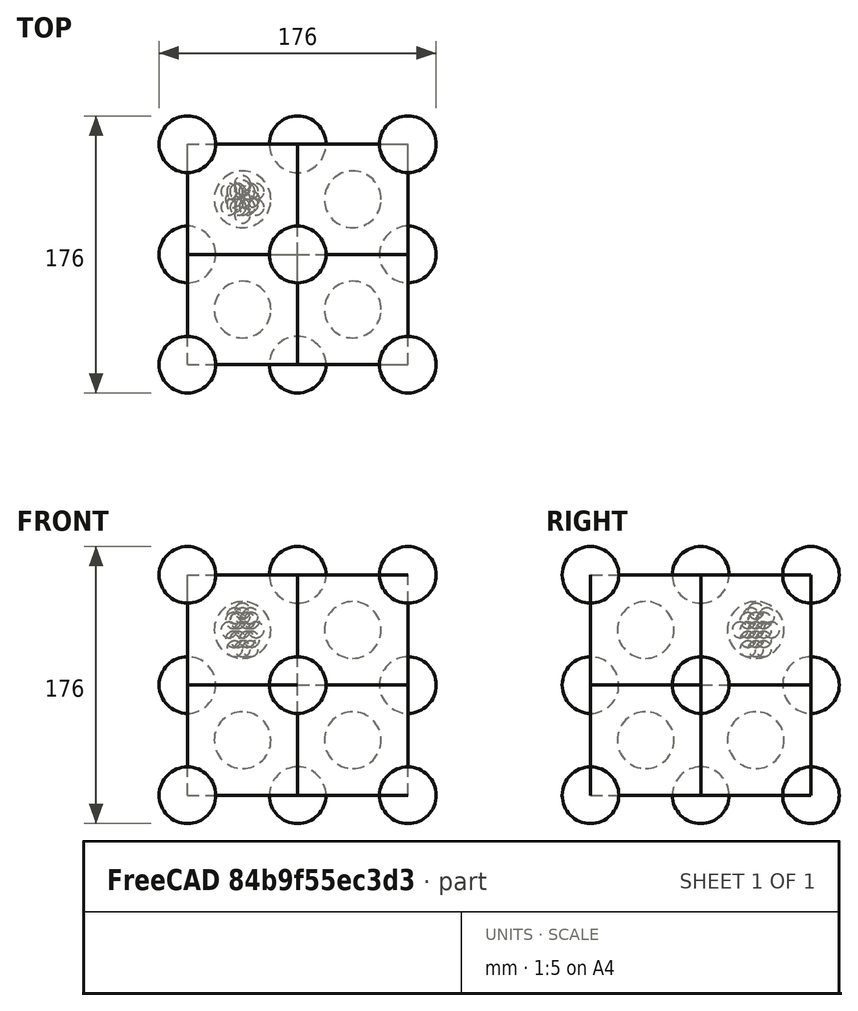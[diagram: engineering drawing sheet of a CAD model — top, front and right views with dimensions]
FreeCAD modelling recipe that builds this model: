
FCSTD DOCUMENT  (FreeCAD 0.16R6707 (Git))
Label: si-cristal
License: All rights reserved
LicenseURL: http://en.wikipedia.org/wiki/All_rights_reserved
objects: Part::Feature×45, Part::Sphere×10, Part::Part2DObjectPython×4, App::DocumentObjectGroup×2, Part::Box×1, Part::FeaturePython×1
note: 61 computed .brp shape members not serialized (recipe doc carries the construction recipe); baked Part::Feature solids carry a one-line shape summary decoded from their .brp

FEATURE [Part::Feature] Sphere001
  Placement = pos=(0,-10,0) rot=(0,0,1;0rad)
  shape: bbox 10 x 10 x 10 mm, 1 faces (baked)
FEATURE [Part::Feature] Sphere002
  Placement = pos=(-8.66025,-5,0) rot=(0,0,1;0rad)
  shape: bbox 10 x 10 x 10 mm, 1 faces (baked)
FEATURE [Part::Feature] Sphere003
  Placement = pos=(-8.66025,5,0) rot=(0,0,1;0rad)
  shape: bbox 10 x 10 x 10 mm, 1 faces (baked)
FEATURE [Part::Feature] Sphere004
  Placement = pos=(8.66025,-5,0) rot=(0,0,1;0rad)
  shape: bbox 10 x 10 x 10 mm, 1 faces (baked)
FEATURE [Part::Feature] Sphere005
  Placement = pos=(8.66025,5,0) rot=(0,0,1;0rad)
  shape: bbox 10 x 10 x 10 mm, 1 faces (baked)
FEATURE [Part::Feature] Sphere006
  Placement = pos=(4e-12,10,0) rot=(0,0,1;0rad)
  shape: bbox 10 x 10 x 10 mm, 1 faces (baked)
FEATURE [Part::Sphere] Sphere007  label="Center"
  Angle1 = -90
  Angle2 = 90
  Angle3 = 360
  Radius = 5
FEATURE [Part::Feature] Sphere  label="Sphere030"
  Placement = pos=(-3,5,6) rot=(0,0,1;0rad)
  shape: bbox 10 x 10 x 10 mm, 1 faces (baked)
FEATURE [Part::Feature] Sphere008  label="Sphere031"
  Placement = pos=(2.83013,5.09808,6) rot=(0,0,1;0rad)
  shape: bbox 10 x 10 x 10 mm, 1 faces (baked)
FEATURE [Part::Feature] Sphere009  label="Sphere032"
  Placement = pos=(5.83013,0.0980762,6) rot=(0,0,1;0rad)
  shape: bbox 10 x 10 x 10 mm, 1 faces (baked)
FEATURE [Part::Feature] Sphere010  label="Sphere033"
  Placement = pos=(3,-5,6) rot=(0,0,1;0rad)
  shape: bbox 10 x 10 x 10 mm, 1 faces (baked)
FEATURE [Part::Feature] Sphere011  label="Sphere034"
  Placement = pos=(-2.83013,-5.09808,6) rot=(0,0,1;0rad)
  shape: bbox 10 x 10 x 10 mm, 1 faces (baked)
FEATURE [Part::Feature] Sphere012  label="Sphere035"
  Placement = pos=(-5.83013,-0.0980762,6) rot=(0,0,1;0rad)
  shape: bbox 10 x 10 x 10 mm, 1 faces (baked)
FEATURE [Part::Feature] Sphere013  label="Sphere036"
  Placement = pos=(-3,5,-6) rot=(0,0,1;0rad)
  shape: bbox 10 x 10 x 10 mm, 1 faces (baked)
FEATURE [Part::Feature] Sphere014  label="Sphere037"
  Placement = pos=(2.83013,5.09808,-6) rot=(0,0,1;0rad)
  shape: bbox 10 x 10 x 10 mm, 1 faces (baked)
FEATURE [Part::Feature] Sphere015  label="Sphere038"
  Placement = pos=(-2.83013,-5.09808,-6) rot=(0,0,1;0rad)
  shape: bbox 10 x 10 x 10 mm, 1 faces (baked)
FEATURE [Part::Feature] Sphere016  label="Sphere039"
  Placement = pos=(5.83013,0.0980762,-6) rot=(0,0,1;0rad)
  shape: bbox 10 x 10 x 10 mm, 1 faces (baked)
FEATURE [Part::Feature] Sphere017  label="Sphere015"
  Placement = pos=(3,-5,-6) rot=(0,0,1;0rad)
  shape: bbox 10 x 10 x 10 mm, 1 faces (baked)
FEATURE [Part::Feature] Sphere018  label="Sphere040"
  Placement = pos=(-5.83013,-0.0980762,-6) rot=(0,0,1;0rad)
  shape: bbox 10 x 10 x 10 mm, 1 faces (baked)
FEATURE [Part::Sphere] Sphere019
  Angle1 = -90
  Angle2 = 90
  Angle3 = 360
  Placement = pos=(0,0,12) rot=(0,0,1;0rad)
  Radius = 5
FEATURE [Part::Sphere] Sphere020  label="Sphere041"
  Angle1 = -90
  Angle2 = 90
  Angle3 = 360
  Placement = pos=(0,0,-12) rot=(0,0,1;0rad)
  Radius = 5
FEATURE [Part::Sphere] Sphere021  label="Sphere042"
  Angle1 = -90
  Angle2 = 90
  Angle3 = 360
  Placement = pos=(0,7,9) rot=(0,0,1;0rad)
  Radius = 5
FEATURE [Part::Sphere] Sphere022  label="Sphere043"
  Angle1 = -90
  Angle2 = 90
  Angle3 = 360
  Placement = pos=(-5,-3,9) rot=(0,0,1;0rad)
  Radius = 5
FEATURE [Part::Sphere] Sphere023  label="Sphere044"
  Angle1 = -90
  Angle2 = 90
  Angle3 = 360
  Placement = pos=(5,-3,9) rot=(0,0,1;0rad)
  Radius = 5
FEATURE [Part::Sphere] Sphere024  label="Sphere045"
  Angle1 = -90
  Angle2 = 90
  Angle3 = 360
  Placement = pos=(-5,5,-12) rot=(0,0,1;0rad)
  Radius = 5
FEATURE [Part::Sphere] Sphere025  label="Sphere046"
  Angle1 = -90
  Angle2 = 90
  Angle3 = 360
  Placement = pos=(5,5,-12) rot=(0,0,1;0rad)
  Radius = 5
FEATURE [Part::Sphere] Sphere026  label="Sphere047"
  Angle1 = -90
  Angle2 = 90
  Angle3 = 360
  Placement = pos=(0,-5,-12) rot=(0,0,1;0rad)
  Radius = 5
FEATURE [App::DocumentObjectGroup] Group  label="core"
  Group = -> [Sphere001,Sphere002,Sphere003,Sphere004,Sphere005,Sphere006,Sphere007,Sphere,Sphere008,Sphere009,Sphere010,Sphere011,Sphere012,Sphere013,Sphere014,Sphere015,Sphere016,Sphere017,Sphere018,Sphere019,Sphere020,Sphere021,Sphere022,Sphere023,Sphere024,Sphere025,Sphere026]
FEATURE [Part::Part2DObjectPython] Polygon  # Draft 2D object (typed FeaturePython)
  ChamferSize = 0
  DrawMode = 0
  FacesNumber = 3
  FilletRadius = 0
  MakeFace = false
  Placement = pos=(0,0,-31) rot=(0,0,1;0rad)
  Radius = 50
FEATURE [Part::Part2DObjectPython] Line002  # Draft 2D object (typed FeaturePython)
  ChamferSize = 0
  Closed = false
  End = (-25,-43.3013,-31)
  FilletRadius = 0
  Length = 87.0816
  MakeFace = true
  Placement = pos=(0,0,-31) rot=(0,0,1;0rad)
  Points = (2) [(1.07885,0,70.9091),(-25,-43.3013,0)]
  Start = (1.07885,0,39.9091)
  Subdivisions = 0
FEATURE [Part::Part2DObjectPython] Line003  # Draft 2D object (typed FeaturePython)
  ChamferSize = 0
  Closed = false
  End = (50,0,-31)
  FilletRadius = 0
  Length = 86.1474
  MakeFace = true
  Placement = pos=(0,0,-31) rot=(0,0,1;0rad)
  Points = (2) [(1.07885,0,70.9091),(50,1.53081e-15,0)]
  Start = (1.07885,0,39.9091)
  Subdivisions = 0
FEATURE [Part::Part2DObjectPython] Line004  # Draft 2D object (typed FeaturePython)
  ChamferSize = 0
  Closed = false
  End = (-25,43.3013,-31)
  FilletRadius = 0
  Length = 87.0816
  MakeFace = true
  Placement = pos=(0,0,-31) rot=(0,0,1;0rad)
  Points = (2) [(1.07885,0,70.9091),(-25,43.3013,0)]
  Start = (1.07885,0,39.9091)
  Subdivisions = 0
FEATURE [App::DocumentObjectGroup] Group001  label="tetrahedron"
  Group = -> [Line002,Line003,Line004,Polygon]
FEATURE [Part::Box] Box  label="Cube"
  Height = 70
  Length = 70
  Placement = pos=(-35,-35,-35) rot=(0,0,1;0rad)
  Width = 70
FEATURE [Part::Sphere] Sphere027  label="Sphere"
  Angle1 = -90
  Angle2 = 90
  Angle3 = 360
  Radius = 18
FEATURE [Part::FeaturePython] Clone  label="Clone of Sphere"  # Draft clone (typed FeaturePython)
  Objects = -> [Sphere027]
  Placement = pos=(-35,35,35) rot=(0,0,1;0rad)
  Scale = (1,1,1)
FEATURE [Part::Feature] Clone001  label="Clone of Sphere001"
  Placement = pos=(-35,-35,-35) rot=(0,0,1;0rad)
  shape: bbox 36 x 36 x 36 mm, 1 faces (baked)
FEATURE [Part::Feature] Clone002  label="Clone of Sphere002"
  Placement = pos=(35,-35,35) rot=(0,0,1;0rad)
  shape: bbox 36 x 36 x 36 mm, 1 faces (baked)
FEATURE [Part::Feature] Clone003  label="Clone of Sphere003"
  Placement = pos=(35,35,-35) rot=(0,0,1;0rad)
  shape: bbox 36 x 36 x 36 mm, 1 faces (baked)
FEATURE [Part::Feature] Clone004  label="Clone of Sphere004"
  Placement = pos=(35,-35,-105) rot=(0,0,1;0rad)
  shape: bbox 36 x 36 x 36 mm, 1 faces (baked)
FEATURE [Part::Feature] Sphere028  label="Sphere048"
  Placement = pos=(70,0,-70) rot=(0,0,1;0rad)
  shape: bbox 36 x 36 x 36 mm, 1 faces (baked)
FEATURE [Part::Feature] Clone005  label="Clone of Sphere005"
  Placement = pos=(105,-35,-35) rot=(0,0,1;0rad)
  shape: bbox 36 x 36 x 36 mm, 1 faces (baked)
FEATURE [Part::Feature] Clone006  label="Clone of Sphere006"
  Placement = pos=(105,35,-105) rot=(0,0,1;0rad)
  shape: bbox 36 x 36 x 36 mm, 1 faces (baked)
FEATURE [Part::Feature] Box001  label="Cube001"
  Placement = pos=(35,-35,-105) rot=(0,0,1;0rad)
  shape: bbox 70 x 70 x 70 mm, 6 faces (baked)
FEATURE [Part::Feature] Clone007  label="Clone of Sphere007"
  Placement = pos=(-35,-105,-105) rot=(0,0,1;0rad)
  shape: bbox 36 x 36 x 36 mm, 1 faces (baked)
FEATURE [Part::Feature] Clone008  label="Clone of Sphere008"
  Placement = pos=(35,-105,-35) rot=(0,0,1;0rad)
  shape: bbox 36 x 36 x 36 mm, 1 faces (baked)
FEATURE [Part::Feature] Sphere029  label="Sphere049"
  Placement = pos=(0,-70,-70) rot=(0,0,1;0rad)
  shape: bbox 36 x 36 x 36 mm, 1 faces (baked)
FEATURE [Part::Feature] Box002  label="Cube002"
  Placement = pos=(-35,-105,-105) rot=(0,0,1;0rad)
  shape: bbox 70 x 70 x 70 mm, 6 faces (baked)
FEATURE [Part::Feature] Sphere030  label="Sphere050"
  Placement = pos=(0,-70,0) rot=(0,0,1;0rad)
  shape: bbox 36 x 36 x 36 mm, 1 faces (baked)
FEATURE [Part::Feature] Box003  label="Cube003"
  Placement = pos=(-35,-105,-35) rot=(0,0,1;0rad)
  shape: bbox 70 x 70 x 70 mm, 6 faces (baked)
FEATURE [Part::Feature] Clone009  label="Clone of Sphere009"
  Placement = pos=(-35,-105,35) rot=(0,0,1;0rad)
  shape: bbox 36 x 36 x 36 mm, 1 faces (baked)
FEATURE [Part::Feature] Sphere031  label="Sphere051"
  Placement = pos=(70,0,0) rot=(0,0,1;0rad)
  shape: bbox 36 x 36 x 36 mm, 1 faces (baked)
FEATURE [Part::Feature] Box004  label="Cube004"
  Placement = pos=(35,-35,-35) rot=(0,0,1;0rad)
  shape: bbox 70 x 70 x 70 mm, 6 faces (baked)
FEATURE [Part::Feature] Clone012  label="Clone of Sphere012"
  Placement = pos=(105,35,35) rot=(0,0,1;0rad)
  shape: bbox 36 x 36 x 36 mm, 1 faces (baked)
FEATURE [Part::Feature] Box005  label="Cube005"
  Placement = pos=(35,-105,-105) rot=(0,0,1;0rad)
  shape: bbox 70 x 70 x 70 mm, 6 faces (baked)
FEATURE [Part::Feature] Clone013  label="Clone of Sphere013"
  Placement = pos=(105,-105,-105) rot=(0,0,1;0rad)
  shape: bbox 36 x 36 x 36 mm, 1 faces (baked)
FEATURE [Part::Feature] Box006  label="Cube006"
  Placement = pos=(35,-105,-35) rot=(0,0,1;0rad)
  shape: bbox 70 x 70 x 70 mm, 6 faces (baked)
FEATURE [Part::Feature] Clone014  label="Clone of Sphere014"
  Placement = pos=(105,-105,35) rot=(0,0,1;0rad)
  shape: bbox 36 x 36 x 36 mm, 1 faces (baked)
FEATURE [Part::Feature] Sphere032  label="Sphere052"
  Placement = pos=(70,-70,-70) rot=(0,0,1;0rad)
  shape: bbox 36 x 36 x 36 mm, 1 faces (baked)
FEATURE [Part::Feature] Box007  label="Cube007"
  Placement = pos=(-35,-35,-105) rot=(0,0,1;0rad)
  shape: bbox 70 x 70 x 70 mm, 6 faces (baked)
FEATURE [Part::Feature] Clone015  label="Clone of Sphere015"
  Placement = pos=(-35,35,-105) rot=(0,0,1;0rad)
  shape: bbox 36 x 36 x 36 mm, 1 faces (baked)
FEATURE [Part::Feature] Sphere033  label="Sphere053"
  Placement = pos=(0,0,-70) rot=(0,0,1;0rad)
  shape: bbox 36 x 36 x 36 mm, 1 faces (baked)
FEATURE [Part::Feature] Sphere034  label="Sphere054"
  Placement = pos=(70,-70,0) rot=(0,0,1;0rad)
  shape: bbox 36 x 36 x 36 mm, 1 faces (baked)
